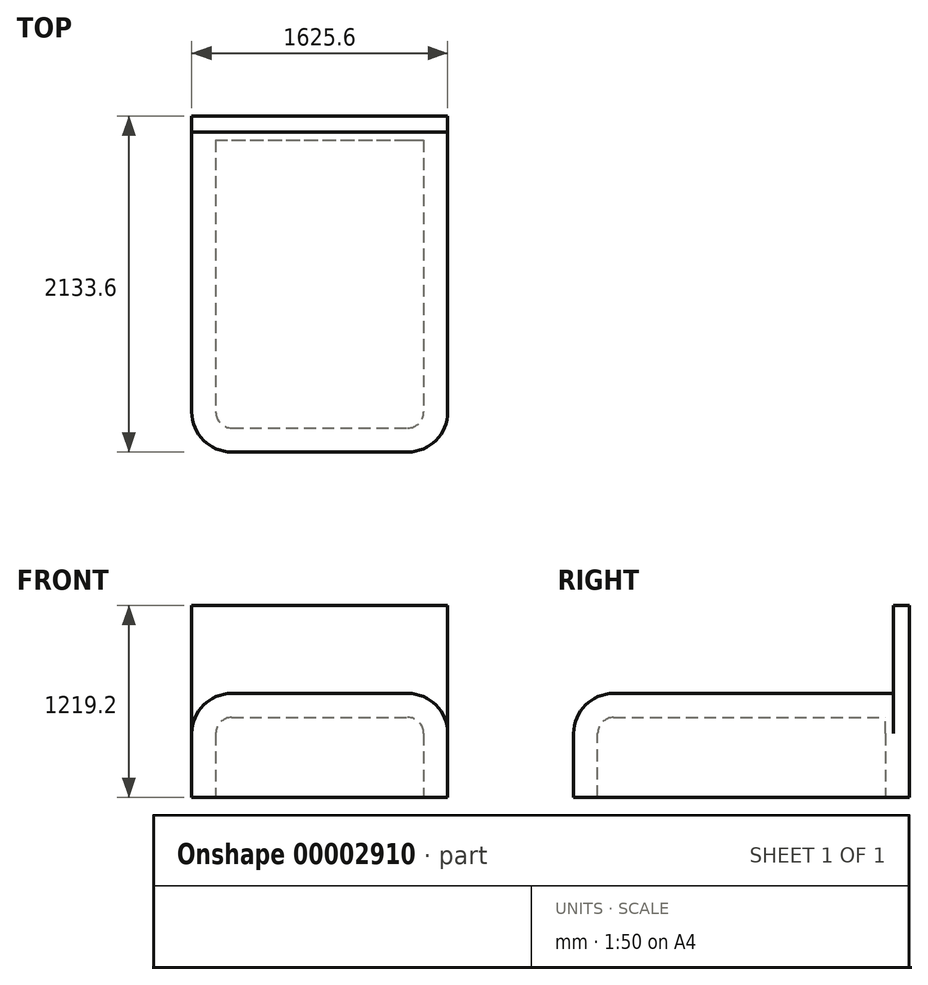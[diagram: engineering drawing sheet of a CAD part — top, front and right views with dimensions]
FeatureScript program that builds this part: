
annotation { "Feature Type Name" : "Feature", "Feature Type Description" : "" }
export const myFeature = defineFeature(function(context is Context, id is Id, definition is map)
    precondition{}
    {
        {
            var Q0;
            Q0=qCreatedBy(makeId("Top.planeOp"),FACE);
            var sketch = newSketch(context, id + "F0", { "sketchPlane" : qUnion([Q0])});
            skLineSegment(sketch, "E0.bottom", {"start": v(-767.69, 1058.94) * mm, "end": v(857.91, 1058.94) * mm});
            skLineSegment(sketch, "E0.top", {"start": v(-767.69, -1074.66) * mm, "end": v(857.91, -1074.66) * mm});
            skLineSegment(sketch, "E0.left", {"start": v(-767.69, 1058.94) * mm, "end": v(-767.69, -1074.66) * mm});
            skLineSegment(sketch, "E0.right", {"start": v(857.91, 1058.94) * mm, "end": v(857.91, -1074.66) * mm});
            skSolve(sketch);
        }
        {
            var Q0;
            Q0=makeQuery(id+"F0.imprint","IMPRINT",FACE,{"disambiguationData":[TD([[makeQuery(id+"F0.imprint","IMPRINT",EDGE,{"derivedFrom":sQuery(id+"F0.wireOp",EDGE,"E0.bottom")}),-1.0]])]});
            extrude(context, id + "F1", {"entities" : qUnion([Q0]), "depth" : 660.4 * mm});
        }
        {
            var Q0;
            Q0=makeQuery(id+"F1.opExtrude","CAP_EDGE",EDGE,{"disambiguationData":[OSD([sQuery(id+"F0.wireOp",EDGE,"E0.left")])],"isStart":false});
            var Q1;
            Q1=makeQuery(id+"F1.opExtrude","CAP_EDGE",EDGE,{"disambiguationData":[OSD([sQuery(id+"F0.wireOp",EDGE,"E0.top")])],"isStart":false});
            var Q2;
            Q2=makeQuery(id+"F1.opExtrude","CAP_EDGE",EDGE,{"disambiguationData":[OSD([sQuery(id+"F0.wireOp",EDGE,"E0.right")])],"isStart":false});
            fillet(context, id + "F2", {"entities" : qUnion([Q0, Q1, Q2]), "radius" : 254 * mm, "tangentPropagation" : true, "allowEdgeOverflow" : false});
        }
        {
            var Q0;
            Q0=makeQuery(id+"F1.opExtrude","CAP_FACE",FACE,{"disambiguationData":[OSD([sQuery(id+"F0.wireOp",EDGE,"E0.bottom"),sQuery(id+"F0.wireOp",EDGE,"E0.top"),sQuery(id+"F0.wireOp",EDGE,"E0.left"),sQuery(id+"F0.wireOp",EDGE,"E0.right")])],"isStart":true});
            var sketch = newSketch(context, id + "F3", { "sketchPlane" : qUnion([Q0])});
            skLineSegment(sketch, "E1.bottom", {"start": v(-767.69, -1058.94) * mm, "end": v(857.91, -1058.94) * mm});
            skLineSegment(sketch, "E1.top", {"start": v(-767.69, -957.34) * mm, "end": v(857.91, -957.34) * mm});
            skLineSegment(sketch, "E1.left", {"start": v(-767.69, -1058.94) * mm, "end": v(-767.69, -957.34) * mm});
            skLineSegment(sketch, "E1.right", {"start": v(857.91, -1058.94) * mm, "end": v(857.91, -957.34) * mm});
            skSolve(sketch);
        }
        {
            var Q0;
            Q0 = qSketchRegion(id + "F3", true);
            extrude(context, id + "F4", {"entities" : qUnion([Q0]), "operationType" : NewBodyOperationType.ADD, "oppositeDirection" : true, "depth" : 1219.2 * mm});
        }
        {
            var Q0;
            Q0=makeQuery(id+"F1.opExtrude","SWEPT_EDGE",EDGE,{"disambiguationData":[OSD([sQuery(id+"F0.wireOp",EDGE,"E0.top"),sQuery(id+"F0.wireOp",EDGE,"E0.right")])]});
            var Q1;
            Q1=makeQuery(id+"F1.opExtrude","SWEPT_EDGE",EDGE,{"disambiguationData":[OSD([sQuery(id+"F0.wireOp",EDGE,"E0.top"),sQuery(id+"F0.wireOp",EDGE,"E0.left")])]});
            fillet(context, id + "F5", {"entities" : qUnion([Q0, Q1]), "radius" : 254 * mm, "tangentPropagation" : true, "allowEdgeOverflow" : false});
        }
        {
            var Q0;
            Q0=makeQuery(id+"F1.opExtrude","CAP_FACE",FACE,{"disambiguationData":[OSD([sQuery(id+"F0.wireOp",EDGE,"E0.bottom"),sQuery(id+"F0.wireOp",EDGE,"E0.top"),sQuery(id+"F0.wireOp",EDGE,"E0.left"),sQuery(id+"F0.wireOp",EDGE,"E0.right")])],"isStart":true});
            shell(context, id + "F6", {"entities" : qUnion([Q0]), "thickness" : 152.4 * mm});
        }
    });
